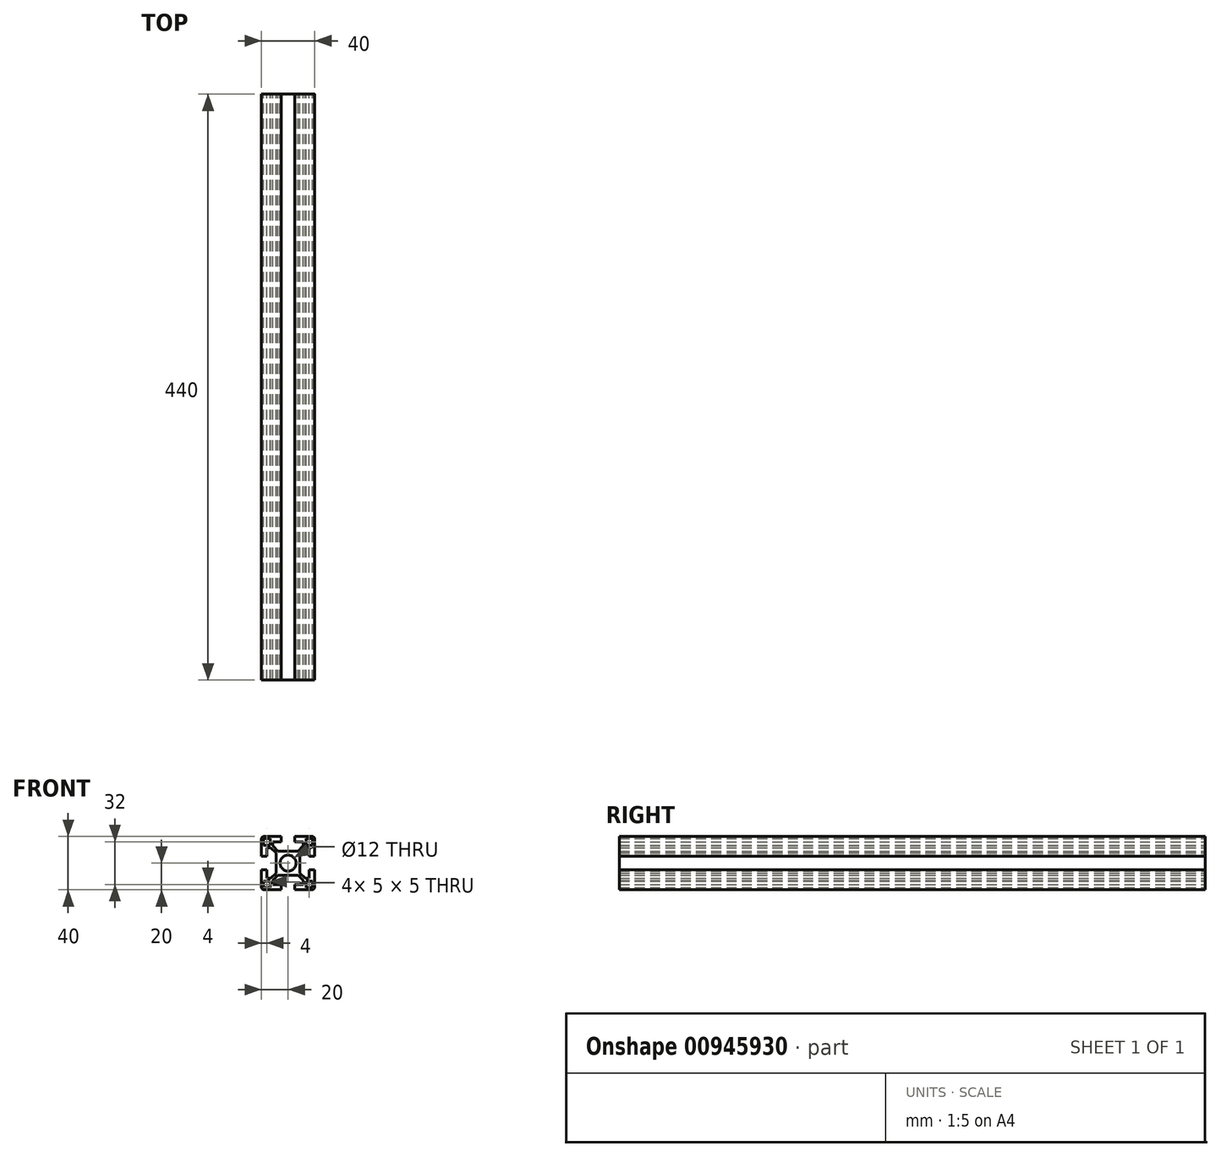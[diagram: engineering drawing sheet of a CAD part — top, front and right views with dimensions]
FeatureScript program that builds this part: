
annotation { "Feature Type Name" : "Feature", "Feature Type Description" : "" }
export const myFeature = defineFeature(function(context is Context, id is Id, definition is map)
    precondition{}
    {
        {
            var Q0;
            Q0=qCreatedBy(makeId("Front.planeOp"),FACE);
            var sketch = newSketch(context, id + "F0", { "sketchPlane" : qUnion([Q0])});
            skLineSegment(sketch, "E0.bottom", {"start": v(18, -20) * mm, "end": v(5, -20) * mm});
            skLineSegment(sketch, "E0.top", {"start": v(18, 20) * mm, "end": v(5, 20) * mm});
            skLineSegment(sketch, "E0.left", {"start": v(20, -18) * mm, "end": v(20, -5) * mm});
            skLineSegment(sketch, "E0.right", {"start": v(-20, -18) * mm, "end": v(-20, -5) * mm});
            skPoint(sketch, "E0.middle", {"position": v(0, 0) * mm});
            skLineSegment(sketch, "E1", {"start": v(0, 20) * mm, "end": v(0, -20) * mm, "construction": true});
            skLineSegment(sketch, "E2", {"start": v(-5, 20) * mm, "end": v(-5, 16) * mm});
            skLineSegment(sketch, "E3", {"start": v(-5, 16) * mm, "end": v(-11.5, 16) * mm});
            skCircle(sketch, "E4", {"center": v(0, 0) * mm, "radius": 6 * mm});
            skPoint(sketch, "E5.visualSharp", {"position": v(-20, 20) * mm});
            skArc(sketch, "E5.filletArc", {"start": v(-18, 20) * mm, "mid": v(-19.41, 19.41) * mm, "end": v(-20, 18) * mm});
            skPoint(sketch, "E6.visualSharp", {"position": v(20, 20) * mm});
            skArc(sketch, "E6.filletArc", {"start": v(20, 18) * mm, "mid": v(19.41, 19.41) * mm, "end": v(18, 20) * mm});
            skPoint(sketch, "E7.visualSharp", {"position": v(20, -20) * mm});
            skArc(sketch, "E7.filletArc", {"start": v(18, -20) * mm, "mid": v(19.41, -19.41) * mm, "end": v(20, -18) * mm});
            skPoint(sketch, "E8.visualSharp", {"position": v(-20, -20) * mm});
            skArc(sketch, "E8.filletArc", {"start": v(-20, -18) * mm, "mid": v(-19.41, -19.41) * mm, "end": v(-18, -20) * mm});
            skLineSegment(sketch, "E9", {"start": v(-7, 7) * mm, "end": v(-18, 18) * mm, "construction": true});
            skLineSegment(sketch, "E10.bottom", {"start": v(-13.5, 13.5) * mm, "end": v(-18.5, 13.5) * mm});
            skLineSegment(sketch, "E10.top", {"start": v(-13.5, 18.5) * mm, "end": v(-18.5, 18.5) * mm});
            skLineSegment(sketch, "E10.left", {"start": v(-13.5, 13.5) * mm, "end": v(-13.5, 18.5) * mm});
            skLineSegment(sketch, "E10.right", {"start": v(-18.5, 13.5) * mm, "end": v(-18.5, 18.5) * mm});
            skPoint(sketch, "E10.middle", {"position": v(-16, 16) * mm});
            skLineSegment(sketch, "E11.MirrorCS", {"start": v(5, 20) * mm, "end": v(5, 16) * mm});
            skLineSegment(sketch, "E12.MirrorCS", {"start": v(5, 16) * mm, "end": v(11.5, 16) * mm});
            skLineSegment(sketch, "E13.MirrorCS", {"start": v(13.5, 13.5) * mm, "end": v(18.5, 13.5) * mm});
            skLineSegment(sketch, "E14.MirrorCS", {"start": v(18.5, 13.5) * mm, "end": v(18.5, 18.5) * mm});
            skLineSegment(sketch, "E15.MirrorCS", {"start": v(13.5, 18.5) * mm, "end": v(18.5, 18.5) * mm});
            skLineSegment(sketch, "E16.MirrorCS", {"start": v(13.5, 13.5) * mm, "end": v(13.5, 18.5) * mm});
            skLineSegment(sketch, "E17", {"start": v(-20, 0) * mm, "end": v(20, 0) * mm, "construction": true});
            skLineSegment(sketch, "E18.trimOffspring", {"start": v(-5, 20) * mm, "end": v(-18, 20) * mm});
            skLineSegment(sketch, "E19", {"start": v(-11.5, 16) * mm, "end": v(-11.5, 12.91) * mm});
            skLineSegment(sketch, "E20", {"start": v(-11.5, 12.91) * mm, "end": v(-7.59, 9) * mm});
            skLineSegment(sketch, "E21", {"start": v(-7.59, 9) * mm, "end": v(0, 9) * mm});
            skLineSegment(sketch, "E22.MirrorCS", {"start": v(11.5, 16) * mm, "end": v(11.5, 12.91) * mm});
            skLineSegment(sketch, "E23.MirrorCS", {"start": v(11.5, 12.91) * mm, "end": v(7.59, 9) * mm});
            skLineSegment(sketch, "E24.MirrorCS", {"start": v(7.59, 9) * mm, "end": v(0, 9) * mm});
            skLineSegment(sketch, "E25.1.0", {"start": v(-20, -5) * mm, "end": v(-16, -5) * mm});
            skLineSegment(sketch, "E25.1.1", {"start": v(-16, -5) * mm, "end": v(-16, -11.5) * mm});
            skLineSegment(sketch, "E25.1.2", {"start": v(-16, -11.5) * mm, "end": v(-12.91, -11.5) * mm});
            skLineSegment(sketch, "E25.1.3", {"start": v(-12.91, -11.5) * mm, "end": v(-9, -7.59) * mm});
            skLineSegment(sketch, "E25.1.4", {"start": v(-9, -7.59) * mm, "end": v(-9, 0) * mm});
            skLineSegment(sketch, "E25.1.5", {"start": v(-9, 7.59) * mm, "end": v(-9, 0) * mm});
            skLineSegment(sketch, "E25.1.6", {"start": v(-12.91, 11.5) * mm, "end": v(-9, 7.59) * mm});
            skLineSegment(sketch, "E25.1.7", {"start": v(-16, 11.5) * mm, "end": v(-12.91, 11.5) * mm});
            skLineSegment(sketch, "E25.1.8", {"start": v(-16, 5) * mm, "end": v(-16, 11.5) * mm});
            skLineSegment(sketch, "E25.1.9", {"start": v(-20, 5) * mm, "end": v(-16, 5) * mm});
            skLineSegment(sketch, "E25.2.0", {"start": v(5, -20) * mm, "end": v(5, -16) * mm});
            skLineSegment(sketch, "E25.2.1", {"start": v(5, -16) * mm, "end": v(11.5, -16) * mm});
            skLineSegment(sketch, "E25.2.2", {"start": v(11.5, -16) * mm, "end": v(11.5, -12.91) * mm});
            skLineSegment(sketch, "E25.2.3", {"start": v(11.5, -12.91) * mm, "end": v(7.59, -9) * mm});
            skLineSegment(sketch, "E25.2.4", {"start": v(7.59, -9) * mm, "end": v(0, -9) * mm});
            skLineSegment(sketch, "E25.2.5", {"start": v(-7.59, -9) * mm, "end": v(0, -9) * mm});
            skLineSegment(sketch, "E25.2.6", {"start": v(-11.5, -12.91) * mm, "end": v(-7.59, -9) * mm});
            skLineSegment(sketch, "E25.2.7", {"start": v(-11.5, -16) * mm, "end": v(-11.5, -12.91) * mm});
            skLineSegment(sketch, "E25.2.8", {"start": v(-5, -16) * mm, "end": v(-11.5, -16) * mm});
            skLineSegment(sketch, "E25.2.9", {"start": v(-5, -20) * mm, "end": v(-5, -16) * mm});
            skLineSegment(sketch, "E26.2.3.0", {"start": v(20, 5) * mm, "end": v(16, 5) * mm});
            skLineSegment(sketch, "E26.3.3.0", {"start": v(16, 5) * mm, "end": v(16, 11.5) * mm});
            skLineSegment(sketch, "E26.6.3.0", {"start": v(16, 11.5) * mm, "end": v(12.91, 11.5) * mm});
            skLineSegment(sketch, "E26.9.3.0", {"start": v(12.91, 11.5) * mm, "end": v(9, 7.59) * mm});
            skLineSegment(sketch, "E26.12.3.0", {"start": v(9, 7.59) * mm, "end": v(9, 0) * mm});
            skLineSegment(sketch, "E26.15.3.0", {"start": v(9, -7.59) * mm, "end": v(9, 0) * mm});
            skLineSegment(sketch, "E26.18.3.0", {"start": v(12.91, -11.5) * mm, "end": v(9, -7.59) * mm});
            skLineSegment(sketch, "E26.21.3.0", {"start": v(16, -11.5) * mm, "end": v(12.91, -11.5) * mm});
            skLineSegment(sketch, "E26.24.3.0", {"start": v(16, -5) * mm, "end": v(16, -11.5) * mm});
            skLineSegment(sketch, "E26.27.3.0", {"start": v(20, -5) * mm, "end": v(16, -5) * mm});
            skLineSegment(sketch, "E27.trimOffspring", {"start": v(-20, 5) * mm, "end": v(-20, 18) * mm});
            skLineSegment(sketch, "E28.trimOffspring", {"start": v(-5, -20) * mm, "end": v(-18, -20) * mm});
            skLineSegment(sketch, "E29.trimOffspring", {"start": v(20, 5) * mm, "end": v(20, 18) * mm});
            skLineSegment(sketch, "E30.MirrorCS", {"start": v(-18.5, -13.5) * mm, "end": v(-18.5, -18.5) * mm});
            skLineSegment(sketch, "E31.MirrorCS", {"start": v(-13.5, -18.5) * mm, "end": v(-18.5, -18.5) * mm});
            skLineSegment(sketch, "E32.MirrorCS", {"start": v(-13.5, -13.5) * mm, "end": v(-13.5, -18.5) * mm});
            skLineSegment(sketch, "E33.MirrorCS", {"start": v(-13.5, -13.5) * mm, "end": v(-18.5, -13.5) * mm});
            skLineSegment(sketch, "E34.MirrorCS", {"start": v(13.5, -13.5) * mm, "end": v(13.5, -18.5) * mm});
            skLineSegment(sketch, "E35.MirrorCS", {"start": v(13.5, -18.5) * mm, "end": v(18.5, -18.5) * mm});
            skLineSegment(sketch, "E36.MirrorCS", {"start": v(18.5, -13.5) * mm, "end": v(18.5, -18.5) * mm});
            skLineSegment(sketch, "E37.MirrorCS", {"start": v(13.5, -13.5) * mm, "end": v(18.5, -13.5) * mm});
            skSolve(sketch);
        }
        {
            var Q0;
            Q0=makeQuery(id+"F0.imprint","IMPRINT",FACE,{"disambiguationData":[TD([[makeQuery(id+"F0.imprint","IMPRINT",EDGE,{"derivedFrom":sQuery(id+"F0.wireOp",EDGE,"E0.bottom")}),-1.0]])]});
            extrude(context, id + "F1", {"entities" : qUnion([Q0]), "depth" : 440 * mm, "offsetDistance" : 25 * mm});
        }
    });
